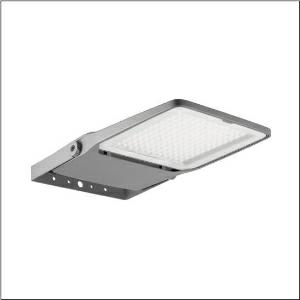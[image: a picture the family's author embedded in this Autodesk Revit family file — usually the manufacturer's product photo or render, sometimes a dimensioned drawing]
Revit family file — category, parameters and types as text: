
# Revit family: floodlight_fl_20_midi___pl61_5xa7682d2c2ac_159a
name_source: partatom
category: Lighting Fixtures
units: mm (PartAtom-declared; Revit-internal decimal feet)

## family parameters
Cut with Voids When Loaded = No
Host = Face
Light Source = No
Part Type = Normal
Room Calculation Point = No
Round Connector Dimension = Use Diameter
Shared = No

## types (1)
- --- (1 x LED 4000K / CRI = 70 (unbekannt), 18200 lm, 4000K)
    Apparent Load = 142 VA
    CIE Flux Codes = 33 65 98 100 100
    Color Rendering = 70
    Color Temperature = 4000K
    Default Elevation = 1800 mm
    Description = Floodlight FL 20 midi, floodlight, primary light control with lens, of plastic, primary optical cover: protective disc, of toughened safety glass, transparent, light distribution: PL61, light emission: direct distribution, primary light characteristic: asymmetric, installation type: surface-mounted, LED High Power LED, rated luminous flux: 18.200 lm, light colour: 740, colour temperature: 4000K, control gear: ECG Plus, control: flexible luminous flux parameterisation, time-dependent luminous flux control, digital communication interface, power reduction, overheat protection, electronic power reduction, with terminal, 5-pole, max. 2.5mm², mains connection: 220..240V, AC, 50/60Hz, rated input power: 142W, LED unit, of diecast aluminium, powder-coated, Siteco® metallic grey (DB 702S), length: 731 mm, width: 450 mm, height: 76mm, housing frame, of diecast aluminium, powder-coated, Siteco® metallic grey (DB 702S), wall fastening, of steel, powder-coated, Siteco® metallic grey (DB 702S), DALIprotection rating (complete): IP66, insulation class (complete): insulation class II (safety insulation), certification: CE, ENEC, VDE, protection symbol: D, permissible ambient temperature for indoor applications: -40..+40°C, permissible ambient temperature for outdoor applications: -40..+50°C, standard: DIN EN 12944, packaging unit: 1 piece

Light Distribution: PL61
    Height = 76 mm
    Lamp = 1 x LED 4000K / CRI >= 70 (unbekannt)
    Lamp Light Flux = 18200 lm
    Lamp count = 1
    Length = 731 mm
    Luminous efficacy = 128 lm/W
    Manufacturer = Siteco
    ModVariant = No
    Model = 5XA7682D2C2AC
    Number of Poles = 1
    OnlyDefault = Yes
    Power Factor = 1
    Product Name = Floodlight FL 20 midi | PL61
    Product group = floodlight | pylon top
    ProductGroupID = 6101
    Protection Class = Protection class II
    Protection Degree = IP 66
    RLX_Detail_Level = 1
    RlxData = <blob elided: 92069 chars, md5=0df9ed3e>
    Socket = socket
    Standby Power = 0 W
    System Light Flux = 18200 lm
    System Power = 142 W
    Type Comments = factory setting: luminous flux: 100 % | dim-lin: 254 | 489 mA
    Type Image = l_1005944.jpg
    URL = http://relux.com
    VarID = @adj_142607
    Voltage = 0 V
    Weight = 0.00 kg
    Width = 450 mm

## geometry (parser evidence)
native form markers: Blend x4, Sweep x12
no freeform markers — native parametric forms only
